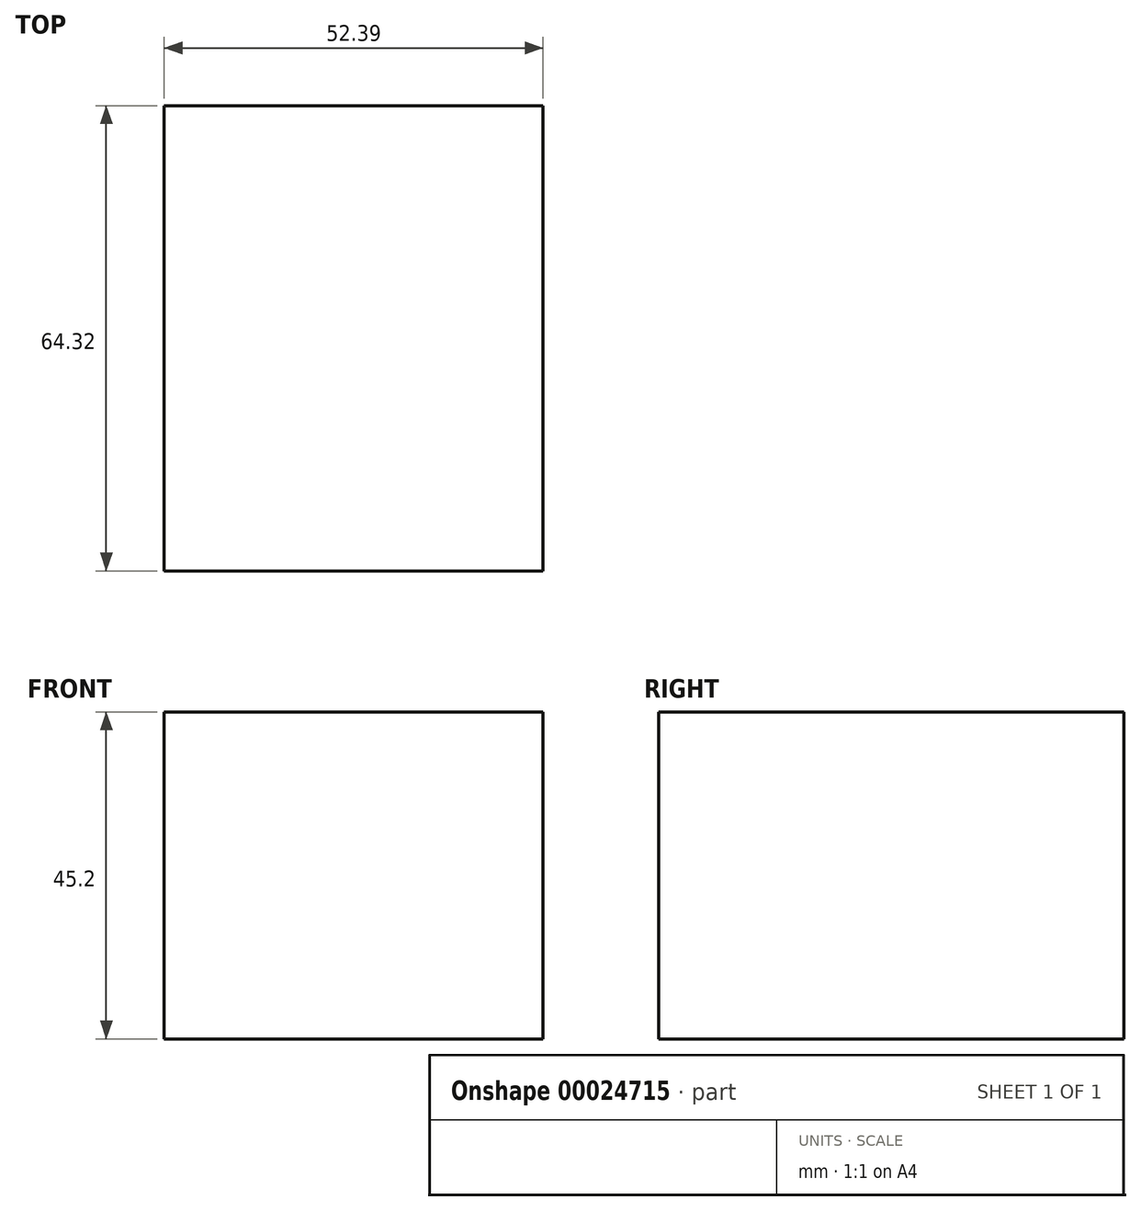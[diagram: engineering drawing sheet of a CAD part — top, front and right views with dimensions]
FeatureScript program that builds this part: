
annotation { "Feature Type Name" : "Feature", "Feature Type Description" : "" }
export const myFeature = defineFeature(function(context is Context, id is Id, definition is map)
    precondition{}
    {
        {
            var Q0;
            Q0=qCreatedBy(makeId("Front.planeOp"),FACE);
            var sketch = newSketch(context, id + "F0", { "sketchPlane" : qUnion([Q0])});
            skLineSegment(sketch, "E0.bottom", {"start": v(-43.77, 36.35) * mm, "end": v(8.62, 36.35) * mm});
            skLineSegment(sketch, "E0.top", {"start": v(-43.77, -8.85) * mm, "end": v(8.62, -8.85) * mm});
            skLineSegment(sketch, "E0.left", {"start": v(-43.77, 36.35) * mm, "end": v(-43.77, -8.85) * mm});
            skLineSegment(sketch, "E0.right", {"start": v(8.62, 36.35) * mm, "end": v(8.62, -8.85) * mm});
            skSolve(sketch);
        }
        {
            var Q0;
            Q0 = qSketchRegion(id + "F0", true);
            extrude(context, id + "F1", {"entities" : qUnion([Q0]), "depth" : 64.32 * mm});
        }
    });
